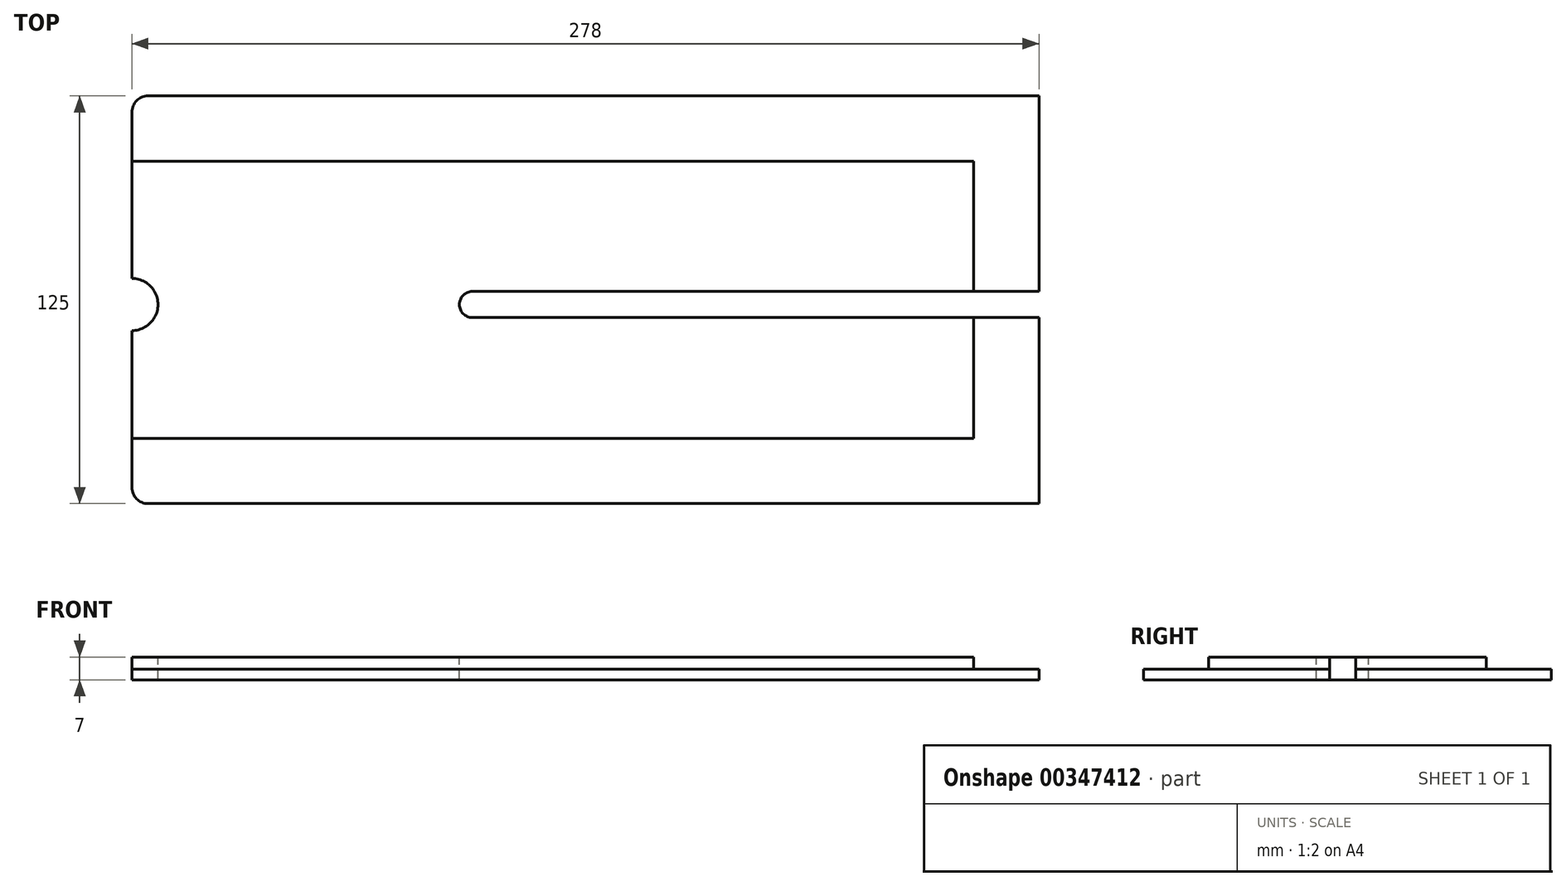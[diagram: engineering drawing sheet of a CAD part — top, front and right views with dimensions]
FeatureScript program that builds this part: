
annotation { "Feature Type Name" : "Feature", "Feature Type Description" : "" }
export const myFeature = defineFeature(function(context is Context, id is Id, definition is map)
    precondition{}
    {
        {
            var Q0;
            Q0=qCreatedBy(makeId("Top.planeOp"),FACE);
            var sketch = newSketch(context, id + "F0", { "sketchPlane" : qUnion([Q0])});
            skLineSegment(sketch, "E0.bottom", {"start": v(-95.37, 63.96) * mm, "end": v(177.63, 63.96) * mm});
            skLineSegment(sketch, "E0.top", {"start": v(-95.37, -61.04) * mm, "end": v(177.63, -61.04) * mm});
            skLineSegment(sketch, "E0.left", {"start": v(-100.37, 58.96) * mm, "end": v(-100.37, -56.04) * mm});
            skLineSegment(sketch, "E0.right", {"start": v(177.63, 63.96) * mm, "end": v(177.63, -61.04) * mm});
            skPoint(sketch, "E1.visualSharp", {"position": v(-100.37, 63.96) * mm});
            skArc(sketch, "E1.filletArc", {"start": v(-95.37, 63.96) * mm, "mid": v(-98.9, 62.5) * mm, "end": v(-100.37, 58.96) * mm});
            skPoint(sketch, "E2.visualSharp", {"position": v(-100.37, -61.04) * mm});
            skArc(sketch, "E2.filletArc", {"start": v(-100.37, -56.04) * mm, "mid": v(-98.9, -59.58) * mm, "end": v(-95.37, -61.04) * mm});
            skPoint(sketch, "E3", {"position": v(-100.37, 1.46) * mm});
            skPoint(sketch, "E4", {"position": v(41.13, 63.96) * mm});
            skSolve(sketch);
        }
        {
            var Q0;
            Q0 = qSketchRegion(id + "F0", true);
            extrude(context, id + "F1", {"entities" : qUnion([Q0]), "depth" : 7 * mm});
        }
        {
            var Q0;
            Q0=makeQuery(id+"F1.opExtrude","CAP_FACE",FACE,{"disambiguationData":[OSD([sQuery(id+"F0.wireOp",EDGE,"E0.bottom"),sQuery(id+"F0.wireOp",EDGE,"E0.top"),sQuery(id+"F0.wireOp",EDGE,"E0.left"),sQuery(id+"F0.wireOp",EDGE,"E0.right"),sQuery(id+"F0.wireOp",EDGE,"E1.filletArc"),sQuery(id+"F0.wireOp",EDGE,"E2.filletArc")])],"isStart":false});
            var sketch = newSketch(context, id + "F2", { "sketchPlane" : qUnion([Q0])});
            skPoint(sketch, "E5.firstSnap0", {"position": v(177.63, 1.46) * mm});
            skLineSegment(sketch, "E5.bottom", {"start": v(177.63, 0) * mm, "end": v(0, 0) * mm});
            skLineSegment(sketch, "E5.top", {"start": v(177.63, -4) * mm, "end": v(4, -4) * mm});
            skLineSegment(sketch, "E5.left", {"start": v(177.63, 0) * mm, "end": v(177.63, -4) * mm});
            skLineSegment(sketch, "E5.right", {"start": v(0, 0) * mm, "end": v(0, 0) * mm});
            skPoint(sketch, "E6.visualSharp", {"position": v(0, -4) * mm});
            skArc(sketch, "E6.filletArc", {"start": v(0, 0) * mm, "mid": v(1.17, -2.83) * mm, "end": v(4, -4) * mm});
            skSolve(sketch);
        }
        {
            var Q0;
            Q0=makeQuery(id+"F2.imprint","IMPRINT",FACE,{"disambiguationData":[TD([[makeQuery(id+"F2.imprint","IMPRINT",EDGE,{"derivedFrom":sQuery(id+"F2.wireOp",EDGE,"E5.bottom")}),1.0]])]});
            var Q1;
            Q1 = qSketchRegion(id + "F2", true);
            extrude(context, id + "F3", {"entities" : qUnion([Q0, Q1]), "operationType" : NewBodyOperationType.REMOVE, "oppositeDirection" : true, "depth" : 25 * mm});
        }
        {
            var Q0;
            Q0=makeQuery(id+"F1.opExtrude","CAP_FACE",FACE,{"disambiguationData":[OSD([sQuery(id+"F0.wireOp",EDGE,"E0.bottom"),sQuery(id+"F0.wireOp",EDGE,"E0.top"),sQuery(id+"F0.wireOp",EDGE,"E0.left"),sQuery(id+"F0.wireOp",EDGE,"E0.right"),sQuery(id+"F0.wireOp",EDGE,"E1.filletArc"),sQuery(id+"F0.wireOp",EDGE,"E2.filletArc")])],"isStart":false});
            var sketch = newSketch(context, id + "F4", { "sketchPlane" : qUnion([Q0])});
            skLineSegment(sketch, "E7.bottom", {"start": v(0, 0) * mm, "end": v(177.63, 0) * mm});
            skLineSegment(sketch, "E7.top", {"start": v(4, 4) * mm, "end": v(177.63, 4) * mm});
            skLineSegment(sketch, "E7.left", {"start": v(0, 0) * mm, "end": v(0, 0) * mm});
            skLineSegment(sketch, "E7.right", {"start": v(177.63, 0) * mm, "end": v(177.63, 4) * mm});
            skPoint(sketch, "E8.visualSharp", {"position": v(0, 4) * mm});
            skArc(sketch, "E8.filletArc", {"start": v(4, 4) * mm, "mid": v(1.17, 2.83) * mm, "end": v(0, 0) * mm});
            skSolve(sketch);
        }
        {
            var Q0;
            Q0 = qSketchRegion(id + "F4", true);
            extrude(context, id + "F5", {"entities" : qUnion([Q0]), "operationType" : NewBodyOperationType.REMOVE, "oppositeDirection" : true, "depth" : 25 * mm});
        }
        {
            var Q0;
            {var subQ2=sQuery(id+"F2.wireOp",EDGE,"E5.bottom");Q0=makeQuery(id+"F2.imprint","IMPRINT",FACE,{"disambiguationData":[TD([[makeQuery(id+"F2.imprint","IMPRINT",EDGE,{"derivedFrom":subQ2}),-1.0]])]});}
            var sketch = newSketch(context, id + "F6", { "sketchPlane" : qUnion([Q0])});
            skCircle(sketch, "E9", {"center": v(-100.35, 0) * mm, "radius": 8 * mm});
            skSolve(sketch);
        }
        {
            var Q0;
            {var subQ0=sQuery(id+"F6.wireOp",EDGE,"E9");var subQ1=makeQuery(id+"F2.imprint","IMPRINT",EDGE,{"derivedFrom":makeQuery(id+"F1.opExtrude","CAP_EDGE",EDGE,{"disambiguationData":[OSD([sQuery(id+"F0.wireOp",EDGE,"E0.left")])],"isStart":false})});var subQ2=makeQuery(id+"F6.imprint","INTERSECT",VERTEX,{"disambiguationData":[OD(0.0)],"derivedFrom":[subQ1,subQ0]});Q0=makeQuery(id+"F6.imprint","IMPRINT",FACE,{"disambiguationData":[TD([[makeQuery(id+"F6.imprint","IMPRINT",EDGE,{"disambiguationData":[TD([[subQ2,1.0]])],"derivedFrom":subQ0}),1.0]])]});}
            extrude(context, id + "F7", {"entities" : qUnion([Q0]), "operationType" : NewBodyOperationType.REMOVE, "oppositeDirection" : true, "depth" : 25 * mm});
        }
        {
            var Q0;
            Q0=makeQuery(id+"F1.opExtrude","CAP_FACE",FACE,{"disambiguationData":[OSD([sQuery(id+"F0.wireOp",EDGE,"E0.bottom"),sQuery(id+"F0.wireOp",EDGE,"E0.top"),sQuery(id+"F0.wireOp",EDGE,"E0.left"),sQuery(id+"F0.wireOp",EDGE,"E0.right"),sQuery(id+"F0.wireOp",EDGE,"E1.filletArc"),sQuery(id+"F0.wireOp",EDGE,"E2.filletArc")])],"isStart":false});
            var sketch = newSketch(context, id + "F8", { "sketchPlane" : qUnion([Q0])});
            skLineSegment(sketch, "E10.bottom", {"start": v(157.63, 63.96) * mm, "end": v(177.63, 63.96) * mm});
            skLineSegment(sketch, "E10.top", {"start": v(157.63, -61.04) * mm, "end": v(177.63, -61.04) * mm});
            skLineSegment(sketch, "E10.left", {"start": v(157.63, 63.96) * mm, "end": v(157.63, -61.04) * mm});
            skLineSegment(sketch, "E10.right", {"start": v(177.63, 63.96) * mm, "end": v(177.63, -61.04) * mm});
            skSolve(sketch);
        }
        {
            var Q0;
            {var subQ0=sQuery(id+"F8.wireOp",EDGE,"E10.bottom");Q0=makeQuery(id+"F8.imprint","IMPRINT",FACE,{"disambiguationData":[TD([[makeQuery(id+"F8.imprint","IMPRINT",EDGE,{"derivedFrom":subQ0}),-1.0]])]});}
            var Q1;
            {var subQ0=sQuery(id+"F8.wireOp",EDGE,"E10.top");Q1=makeQuery(id+"F8.imprint","IMPRINT",FACE,{"disambiguationData":[TD([[makeQuery(id+"F8.imprint","IMPRINT",EDGE,{"derivedFrom":subQ0}),1.0]])]});}
            extrude(context, id + "F9", {"entities" : qUnion([Q0, Q1]), "operationType" : NewBodyOperationType.REMOVE, "oppositeDirection" : true, "depth" : 3.7 * mm});
        }
        {
            var Q0;
            Q0=makeQuery(id+"F1.opExtrude","CAP_FACE",FACE,{"disambiguationData":[OSD([sQuery(id+"F0.wireOp",EDGE,"E0.bottom"),sQuery(id+"F0.wireOp",EDGE,"E0.top"),sQuery(id+"F0.wireOp",EDGE,"E0.left"),sQuery(id+"F0.wireOp",EDGE,"E0.right"),sQuery(id+"F0.wireOp",EDGE,"E1.filletArc"),sQuery(id+"F0.wireOp",EDGE,"E2.filletArc")])],"isStart":false});
            var sketch = newSketch(context, id + "F10", { "sketchPlane" : qUnion([Q0])});
            skLineSegment(sketch, "E11.bottom", {"start": v(157.63, 63.96) * mm, "end": v(-100.37, 63.96) * mm});
            skLineSegment(sketch, "E11.top", {"start": v(157.63, 43.96) * mm, "end": v(-100.37, 43.96) * mm});
            skLineSegment(sketch, "E11.left", {"start": v(157.63, 63.96) * mm, "end": v(157.63, 43.96) * mm});
            skLineSegment(sketch, "E11.right", {"start": v(-100.37, 63.96) * mm, "end": v(-100.37, 43.96) * mm});
            skLineSegment(sketch, "E12.bottom", {"start": v(157.63, -61.04) * mm, "end": v(-100.37, -61.04) * mm});
            skLineSegment(sketch, "E12.top", {"start": v(157.63, -41.04) * mm, "end": v(-100.37, -41.04) * mm});
            skLineSegment(sketch, "E12.left", {"start": v(157.63, -61.04) * mm, "end": v(157.63, -41.04) * mm});
            skLineSegment(sketch, "E12.right", {"start": v(-100.37, -61.04) * mm, "end": v(-100.37, -41.04) * mm});
            skSolve(sketch);
        }
        {
            var Q0;
            {var subQ3=sQuery(id+"F10.wireOp",EDGE,"E11.top");Q0=makeQuery(id+"F10.imprint","IMPRINT",FACE,{"disambiguationData":[TD([[makeQuery(id+"F10.imprint","IMPRINT",EDGE,{"derivedFrom":subQ3}),-1.0]])]});}
            var Q1;
            {var subQ1=sQuery(id+"F10.wireOp",EDGE,"E12.top");Q1=makeQuery(id+"F10.imprint","IMPRINT",FACE,{"disambiguationData":[TD([[makeQuery(id+"F10.imprint","IMPRINT",EDGE,{"derivedFrom":subQ1}),1.0]])]});}
            extrude(context, id + "F11", {"entities" : qUnion([Q0, Q1]), "operationType" : NewBodyOperationType.REMOVE, "oppositeDirection" : true, "depth" : 3.7 * mm});
        }
    });
